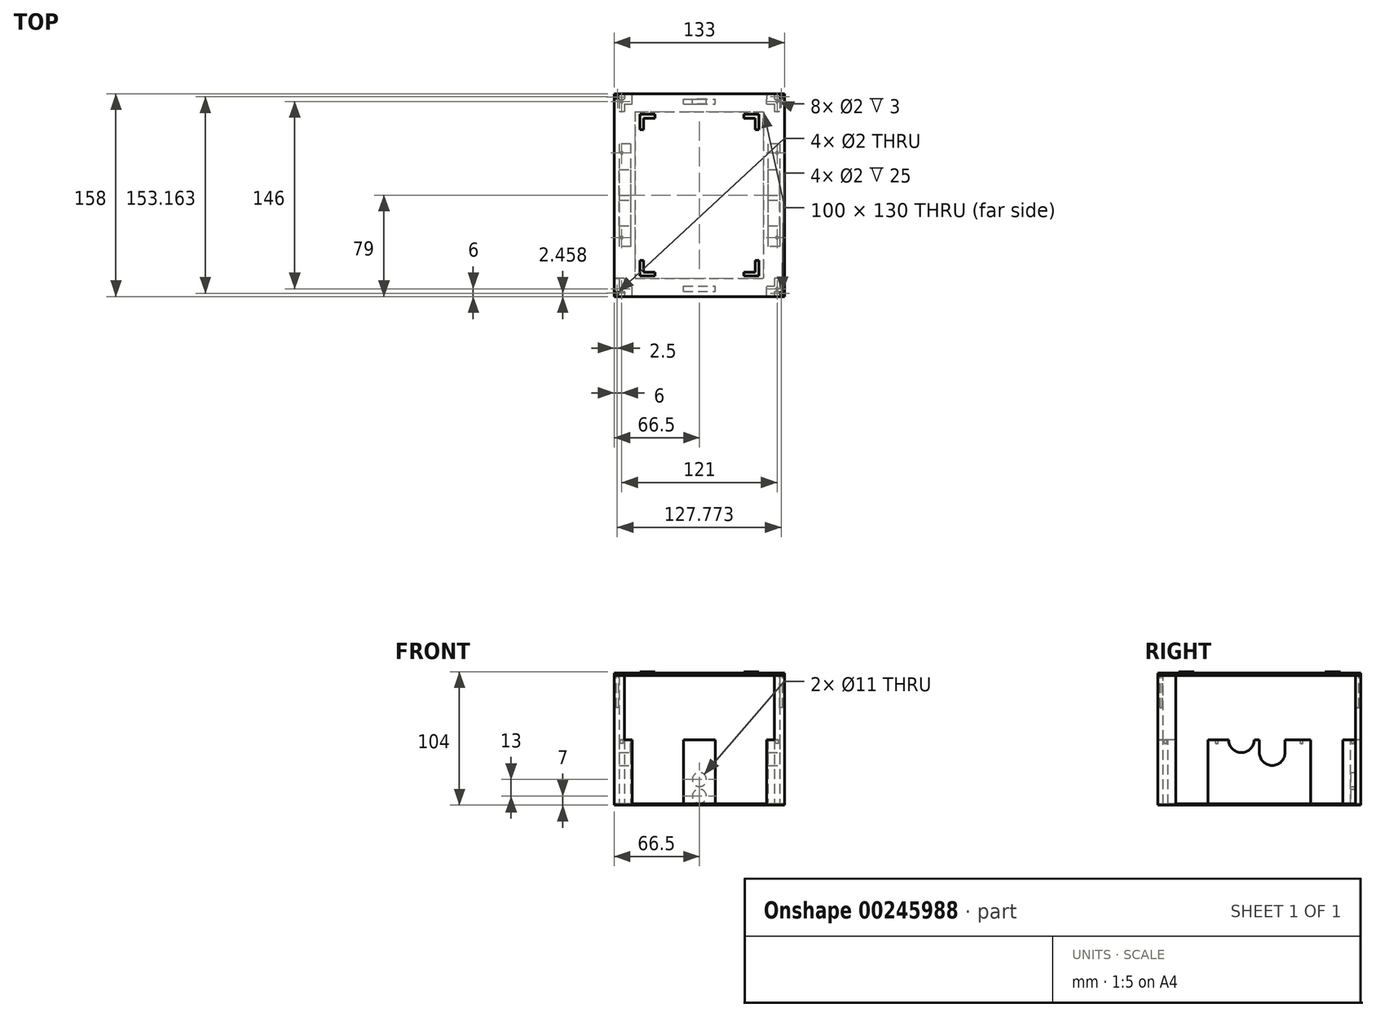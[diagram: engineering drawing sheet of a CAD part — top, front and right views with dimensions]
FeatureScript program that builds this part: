
annotation { "Feature Type Name" : "Feature", "Feature Type Description" : "" }
export const myFeature = defineFeature(function(context is Context, id is Id, definition is map)
    precondition{}
    {
        {
            var Q0;
            Q0=qCreatedBy(makeId("Top.planeOp"),FACE);
            var sketch = newSketch(context, id + "F0", { "sketchPlane" : qUnion([Q0])});
            skLineSegment(sketch, "E0.bottom", {"start": v(-66.5, 79) * mm, "end": v(66.5, 79) * mm});
            skLineSegment(sketch, "E0.top", {"start": v(-66.5, -79) * mm, "end": v(66.5, -79) * mm});
            skLineSegment(sketch, "E0.left", {"start": v(-66.5, 79) * mm, "end": v(-66.5, -79) * mm});
            skLineSegment(sketch, "E0.right", {"start": v(66.5, 79) * mm, "end": v(66.5, -79) * mm});
            skPoint(sketch, "E0.middle", {"position": v(0, 0) * mm});
            skLineSegment(sketch, "E1.bottom", {"start": v(-66.5, 79) * mm, "end": v(-66.5, 79) * mm});
            skLineSegment(sketch, "E1.top", {"start": v(-66.5, 79) * mm, "end": v(-66.5, 79) * mm});
            skLineSegment(sketch, "E1.left", {"start": v(-66.5, 79) * mm, "end": v(-66.5, 79) * mm});
            skLineSegment(sketch, "E1.right", {"start": v(-66.5, 79) * mm, "end": v(-66.5, 79) * mm});
            skLineSegment(sketch, "E2.bottom", {"start": v(-66.5, 79) * mm, "end": v(-62.5, 79) * mm});
            skLineSegment(sketch, "E2.top", {"start": v(-66.5, 79) * mm, "end": v(-62.5, 79) * mm});
            skLineSegment(sketch, "E2.right", {"start": v(-62.5, 79) * mm, "end": v(-62.5, 79) * mm});
            skSolve(sketch);
        }
        {
            var Q0;
            Q0=makeQuery(id+"F0.imprint","IMPRINT",FACE,{"disambiguationData":[TD([[makeQuery(id+"F0.imprint","IMPRINT",EDGE,{"derivedFrom":sQuery(id+"F0.wireOp",EDGE,"E0.bottom")}),-1.0]])]});
            extrude(context, id + "F1", {"entities" : qUnion([Q0]), "depth" : 1 * mm});
        }
        {
            var Q0;
            Q0=makeQuery(id+"F1.opExtrude","CAP_FACE",FACE,{"disambiguationData":[OSD([sQuery(id+"F0.wireOp",EDGE,"E0.bottom"),sQuery(id+"F0.wireOp",EDGE,"E0.top"),sQuery(id+"F0.wireOp",EDGE,"E0.left"),sQuery(id+"F0.wireOp",EDGE,"E0.right")])],"isStart":false});
            var sketch = newSketch(context, id + "F2", { "sketchPlane" : qUnion([Q0])});
            skLineSegment(sketch, "E3.bottom", {"start": v(-62.5, 75) * mm, "end": v(62.5, 75) * mm});
            skLineSegment(sketch, "E3.top", {"start": v(-62.5, -75) * mm, "end": v(62.5, -75) * mm});
            skLineSegment(sketch, "E3.left", {"start": v(-62.5, 75) * mm, "end": v(-62.5, -75) * mm});
            skLineSegment(sketch, "E3.right", {"start": v(62.5, 75) * mm, "end": v(62.5, -75) * mm});
            skPoint(sketch, "E3.middle", {"position": v(0, 0) * mm});
            skSolve(sketch);
        }
        {
            var Q0;
            Q0 = qSketchRegion(id + "F2", true);
            extrude(context, id + "F3", {"entities" : qUnion([Q0]), "operationType" : NewBodyOperationType.ADD, "depth" : 50 * mm});
        }
        {
            var Q0;
            Q0=makeQuery(id+"F3.opExtrude","CAP_FACE",FACE,{"disambiguationData":[OSD([sQuery(id+"F2.wireOp",EDGE,"E3.bottom"),sQuery(id+"F2.wireOp",EDGE,"E3.top"),sQuery(id+"F2.wireOp",EDGE,"E3.left"),sQuery(id+"F2.wireOp",EDGE,"E3.right")])],"isStart":false});
            var sketch = newSketch(context, id + "F4", { "sketchPlane" : qUnion([Q0])});
            skLineSegment(sketch, "E4.bottom", {"start": v(-58.5, 71) * mm, "end": v(58.5, 71) * mm});
            skLineSegment(sketch, "E4.top", {"start": v(-58.5, -71) * mm, "end": v(58.5, -71) * mm});
            skLineSegment(sketch, "E4.left", {"start": v(-58.5, 71) * mm, "end": v(-58.5, -71) * mm});
            skLineSegment(sketch, "E4.right", {"start": v(58.5, 71) * mm, "end": v(58.5, -71) * mm});
            skPoint(sketch, "E4.middle", {"position": v(0, 0) * mm});
            skSolve(sketch);
        }
        {
            var Q0;
            Q0=makeQuery(id+"F4.imprint","IMPRINT",FACE,{"disambiguationData":[TD([[makeQuery(id+"F4.imprint","IMPRINT",EDGE,{"derivedFrom":sQuery(id+"F4.wireOp",EDGE,"E4.bottom")}),-1.0]])]});
            extrude(context, id + "F5", {"entities" : qUnion([Q0]), "operationType" : NewBodyOperationType.REMOVE, "oppositeDirection" : true, "depth" : 50 * mm});
        }
        {
            var Q0;
            Q0=makeQuery(id+"F3.opExtrude","CAP_FACE",FACE,{"disambiguationData":[OSD([sQuery(id+"F2.wireOp",EDGE,"E3.bottom"),sQuery(id+"F2.wireOp",EDGE,"E3.top"),sQuery(id+"F2.wireOp",EDGE,"E3.left"),sQuery(id+"F2.wireOp",EDGE,"E3.right")])],"isStart":false});
            var sketch = newSketch(context, id + "F6", { "sketchPlane" : qUnion([Q0])});
            skCircle(sketch, "E5", {"center": v(-60.5, 73) * mm, "radius": 1 * mm});
            skCircle(sketch, "E6", {"center": v(-60.5, 33) * mm, "radius": 1 * mm});
            skCircle(sketch, "E7", {"center": v(60.5, 73) * mm, "radius": 1 * mm});
            skCircle(sketch, "E8", {"center": v(60.5, 33) * mm, "radius": 1 * mm});
            skCircle(sketch, "E9", {"center": v(-60.5, -33) * mm, "radius": 1 * mm});
            skCircle(sketch, "E10", {"center": v(60.5, -33) * mm, "radius": 1 * mm});
            skCircle(sketch, "E11", {"center": v(-60.5, -73) * mm, "radius": 1 * mm});
            skCircle(sketch, "E12", {"center": v(60.5, -73) * mm, "radius": 1 * mm});
            skSolve(sketch);
        }
        {
            var Q0;
            Q0=makeQuery(id+"F6.imprint","IMPRINT",FACE,{"disambiguationData":[TD([[makeQuery(id+"F6.imprint","IMPRINT",EDGE,{"derivedFrom":sQuery(id+"F6.wireOp",EDGE,"E5")}),1.0]])]});
            var Q1;
            Q1=makeQuery(id+"F6.imprint","IMPRINT",FACE,{"disambiguationData":[TD([[makeQuery(id+"F6.imprint","IMPRINT",EDGE,{"derivedFrom":sQuery(id+"F6.wireOp",EDGE,"E7")}),1.0]])]});
            var Q2;
            Q2=makeQuery(id+"F6.imprint","IMPRINT",FACE,{"disambiguationData":[TD([[makeQuery(id+"F6.imprint","IMPRINT",EDGE,{"derivedFrom":sQuery(id+"F6.wireOp",EDGE,"E8")}),1.0]])]});
            var Q3;
            Q3=makeQuery(id+"F6.imprint","IMPRINT",FACE,{"disambiguationData":[TD([[makeQuery(id+"F6.imprint","IMPRINT",EDGE,{"derivedFrom":sQuery(id+"F6.wireOp",EDGE,"E10")}),1.0]])]});
            var Q4;
            Q4=makeQuery(id+"F6.imprint","IMPRINT",FACE,{"disambiguationData":[TD([[makeQuery(id+"F6.imprint","IMPRINT",EDGE,{"derivedFrom":sQuery(id+"F6.wireOp",EDGE,"E12")}),1.0]])]});
            var Q5;
            Q5=makeQuery(id+"F6.imprint","IMPRINT",FACE,{"disambiguationData":[TD([[makeQuery(id+"F6.imprint","IMPRINT",EDGE,{"derivedFrom":sQuery(id+"F6.wireOp",EDGE,"E11")}),1.0]])]});
            var Q6;
            Q6=makeQuery(id+"F6.imprint","IMPRINT",FACE,{"disambiguationData":[TD([[makeQuery(id+"F6.imprint","IMPRINT",EDGE,{"derivedFrom":sQuery(id+"F6.wireOp",EDGE,"E9")}),1.0]])]});
            var Q7;
            Q7=makeQuery(id+"F6.imprint","IMPRINT",FACE,{"disambiguationData":[TD([[makeQuery(id+"F6.imprint","IMPRINT",EDGE,{"derivedFrom":sQuery(id+"F6.wireOp",EDGE,"E6")}),1.0]])]});
            extrude(context, id + "F7", {"entities" : qUnion([Q0, Q1, Q2, Q3, Q4, Q5, Q6, Q7]), "operationType" : NewBodyOperationType.REMOVE, "oppositeDirection" : true, "depth" : 3 * mm});
        }
        {
            var Q0;
            Q0=makeQuery(id+"F3.opExtrude","SWEPT_FACE",FACE,{"disambiguationData":[OSD([sQuery(id+"F2.wireOp",EDGE,"E3.right")])]});
            var sketch = newSketch(context, id + "F8", { "sketchPlane" : qUnion([Q0])});
            skLineSegment(sketch, "E13.bottom", {"start": v(0, 51) * mm, "end": v(20, 51) * mm});
            skLineSegment(sketch, "E13.top", {"start": v(0, 41) * mm, "end": v(20, 41) * mm});
            skLineSegment(sketch, "E13.left", {"start": v(0, 51) * mm, "end": v(0, 41) * mm});
            skLineSegment(sketch, "E13.right", {"start": v(20, 51) * mm, "end": v(20, 41) * mm});
            skSolve(sketch);
        }
        {
            var Q0;
            Q0=makeQuery(id+"F3.opExtrude","SWEPT_FACE",FACE,{"disambiguationData":[OSD([sQuery(id+"F2.wireOp",EDGE,"E3.right")])]});
            var sketch = newSketch(context, id + "F9", { "sketchPlane" : qUnion([Q0])});
            skCircle(sketch, "E14", {"center": v(10, 41) * mm, "radius": 10 * mm});
            skSolve(sketch);
        }
        {
            var Q0;
            Q0=makeQuery(id+"F8.imprint","IMPRINT",FACE,{"disambiguationData":[TD([[makeQuery(id+"F8.imprint","IMPRINT",EDGE,{"derivedFrom":sQuery(id+"F8.wireOp",EDGE,"E13.bottom")}),1.0]])]});
            extrude(context, id + "F10", {"entities" : qUnion([Q0]), "operationType" : NewBodyOperationType.REMOVE, "endBound" : BoundingType.THROUGH_ALL, "oppositeDirection" : true, "depth" : 25 * mm});
        }
        {
            var Q0;
            Q0=makeQuery(id+"F9.imprint","IMPRINT",FACE,{"disambiguationData":[TD([[makeQuery(id+"F9.imprint","IMPRINT",EDGE,{"derivedFrom":sQuery(id+"F9.wireOp",EDGE,"E14")}),1.0]])]});
            extrude(context, id + "F11", {"entities" : qUnion([Q0]), "operationType" : NewBodyOperationType.REMOVE, "endBound" : BoundingType.THROUGH_ALL, "oppositeDirection" : true, "depth" : 25 * mm});
        }
        {
            var Q0;
            Q0=makeQuery(id+"F3.opExtrude","SWEPT_FACE",FACE,{"disambiguationData":[OSD([sQuery(id+"F2.wireOp",EDGE,"E3.right")])]});
            var sketch = newSketch(context, id + "F12", { "sketchPlane" : qUnion([Q0])});
            skCircle(sketch, "E15", {"center": v(-13.97, 51) * mm, "radius": 10 * mm});
            skSolve(sketch);
        }
        {
            var Q0;
            {var subQ0=sQuery(id+"F12.wireOp",EDGE,"E15");var subQ1=sQuery(id+"F2.wireOp",EDGE,"E3.right");var subQ2=sQuery(id+"F2.wireOp",EDGE,"E3.top");var subQ3=makeQuery(id+"F10.boolean.opBoolean","SPLIT",EDGE,{"disambiguationData":[TD([makeQuery(id+"F3.opExtrude","SWEPT_FACE",FACE,{"disambiguationData":[OSD([subQ2])]})])],"derivedFrom":makeQuery(id+"F3.opExtrude","CAP_EDGE",EDGE,{"disambiguationData":[OSD([subQ1])],"isStart":false})});var subQ4=makeQuery(id+"F12.imprint","INTERSECT",VERTEX,{"disambiguationData":[OD(0.0)],"derivedFrom":[subQ3,subQ0]});Q0=makeQuery(id+"F12.imprint","IMPRINT",FACE,{"disambiguationData":[TD([[makeQuery(id+"F12.imprint","IMPRINT",EDGE,{"disambiguationData":[TD([[subQ4,-1.0]])],"derivedFrom":subQ0}),1.0]])]});}
            extrude(context, id + "F13", {"entities" : qUnion([Q0]), "operationType" : NewBodyOperationType.REMOVE, "endBound" : BoundingType.THROUGH_ALL, "oppositeDirection" : true, "depth" : 25 * mm});
        }
        {
            var Q0;
            Q0=makeQuery(id+"F3.opExtrude","SWEPT_FACE",FACE,{"disambiguationData":[OSD([sQuery(id+"F2.wireOp",EDGE,"E3.bottom")])]});
            var sketch = newSketch(context, id + "F14", { "sketchPlane" : qUnion([Q0])});
            skCircle(sketch, "E16", {"center": v(0, 7) * mm, "radius": 5.5 * mm});
            skCircle(sketch, "E17", {"center": v(0, 20) * mm, "radius": 5.5 * mm});
            skSolve(sketch);
        }
        {
            var Q0;
            Q0=makeQuery(id+"F14.imprint","IMPRINT",FACE,{"disambiguationData":[TD([[makeQuery(id+"F14.imprint","IMPRINT",EDGE,{"derivedFrom":sQuery(id+"F14.wireOp",EDGE,"E17")}),1.0]])]});
            var Q1;
            Q1=makeQuery(id+"F14.imprint","IMPRINT",FACE,{"disambiguationData":[TD([[makeQuery(id+"F14.imprint","IMPRINT",EDGE,{"derivedFrom":sQuery(id+"F14.wireOp",EDGE,"E16")}),1.0]])]});
            extrude(context, id + "F15", {"entities" : qUnion([Q0, Q1]), "operationType" : NewBodyOperationType.REMOVE, "oppositeDirection" : true, "depth" : 4 * mm});
        }
        {
            var Q0;
            Q0=makeQuery(id+"F3.opExtrude","SWEPT_FACE",FACE,{"disambiguationData":[OSD([sQuery(id+"F2.wireOp",EDGE,"E3.bottom")])]});
            var sketch = newSketch(context, id + "F16", { "sketchPlane" : qUnion([Q0])});
            skLineSegment(sketch, "E18.bottom", {"start": v(-52.5, 1) * mm, "end": v(-12.5, 1) * mm});
            skLineSegment(sketch, "E18.top", {"start": v(-52.5, 51) * mm, "end": v(-12.5, 51) * mm});
            skLineSegment(sketch, "E18.left", {"start": v(-52.5, 1) * mm, "end": v(-52.5, 51) * mm});
            skLineSegment(sketch, "E18.right", {"start": v(-12.5, 1) * mm, "end": v(-12.5, 51) * mm});
            skLineSegment(sketch, "E19.bottom", {"start": v(12.5, 51) * mm, "end": v(52.5, 51) * mm});
            skLineSegment(sketch, "E19.top", {"start": v(12.5, 1) * mm, "end": v(52.5, 1) * mm});
            skLineSegment(sketch, "E19.left", {"start": v(12.5, 51) * mm, "end": v(12.5, 1) * mm});
            skLineSegment(sketch, "E19.right", {"start": v(52.5, 51) * mm, "end": v(52.5, 1) * mm});
            skSolve(sketch);
        }
        {
            var Q0;
            Q0=makeQuery(id+"F16.imprint","IMPRINT",FACE,{"disambiguationData":[TD([[makeQuery(id+"F16.imprint","IMPRINT",EDGE,{"derivedFrom":sQuery(id+"F16.wireOp",EDGE,"E18.bottom")}),-1.0]])]});
            var Q1;
            Q1=makeQuery(id+"F16.imprint","IMPRINT",FACE,{"disambiguationData":[TD([[makeQuery(id+"F16.imprint","IMPRINT",EDGE,{"derivedFrom":sQuery(id+"F16.wireOp",EDGE,"E19.bottom")}),1.0]])]});
            extrude(context, id + "F17", {"entities" : qUnion([Q0, Q1]), "operationType" : NewBodyOperationType.REMOVE, "endBound" : BoundingType.THROUGH_ALL, "oppositeDirection" : true, "depth" : 25 * mm});
        }
        {
            var Q0;
            Q0=makeQuery(id+"F3.opExtrude","SWEPT_FACE",FACE,{"disambiguationData":[OSD([sQuery(id+"F2.wireOp",EDGE,"E3.left")])]});
            var sketch = newSketch(context, id + "F18", { "sketchPlane" : qUnion([Q0])});
            skLineSegment(sketch, "E20.bottom", {"start": v(-65, 51) * mm, "end": v(-40, 51) * mm});
            skLineSegment(sketch, "E20.top", {"start": v(-65, 1) * mm, "end": v(-40, 1) * mm});
            skLineSegment(sketch, "E20.left", {"start": v(-65, 51) * mm, "end": v(-65, 1) * mm});
            skLineSegment(sketch, "E20.right", {"start": v(-40, 51) * mm, "end": v(-40, 1) * mm});
            skLineSegment(sketch, "E21.bottom", {"start": v(40, 51) * mm, "end": v(65, 51) * mm});
            skLineSegment(sketch, "E21.top", {"start": v(40, 1) * mm, "end": v(65, 1) * mm});
            skLineSegment(sketch, "E21.left", {"start": v(40, 51) * mm, "end": v(40, 1) * mm});
            skLineSegment(sketch, "E21.right", {"start": v(65, 51) * mm, "end": v(65, 1) * mm});
            skSolve(sketch);
        }
        {
            var Q0;
            Q0=makeQuery(id+"F18.imprint","IMPRINT",FACE,{"disambiguationData":[TD([[makeQuery(id+"F18.imprint","IMPRINT",EDGE,{"derivedFrom":sQuery(id+"F18.wireOp",EDGE,"E20.bottom")}),-1.0]])]});
            var Q1;
            Q1=makeQuery(id+"F18.imprint","IMPRINT",FACE,{"disambiguationData":[TD([[makeQuery(id+"F18.imprint","IMPRINT",EDGE,{"derivedFrom":sQuery(id+"F18.wireOp",EDGE,"E21.bottom")}),-1.0]])]});
            extrude(context, id + "F19", {"entities" : qUnion([Q0, Q1]), "operationType" : NewBodyOperationType.REMOVE, "endBound" : BoundingType.THROUGH_ALL, "oppositeDirection" : true, "depth" : 25 * mm});
        }
        {
            var Q0;
            Q0=makeQuery(id+"F19.boolean.opBoolean","MERGE",FACE,{"derivedFrom":[makeQuery(id+"F17.boolean.opBoolean","MERGE",FACE,{"derivedFrom":[makeQuery(id+"F1.opExtrude","CAP_FACE",FACE,{"disambiguationData":[OSD([sQuery(id+"F0.wireOp",EDGE,"E0.bottom"),sQuery(id+"F0.wireOp",EDGE,"E0.top"),sQuery(id+"F0.wireOp",EDGE,"E0.left"),sQuery(id+"F0.wireOp",EDGE,"E0.right"),sQuery(id+"F0.wireOp",EDGE,"E2.top")])],"isStart":false}),makeQuery(id+"F5.boolean.opBoolean","COPY",FACE,{"derivedFrom":makeQuery(id+"F5.opExtrude","CAP_FACE",FACE,{"disambiguationData":[OSD([sQuery(id+"F4.wireOp",EDGE,"E4.bottom"),sQuery(id+"F4.wireOp",EDGE,"E4.top"),sQuery(id+"F4.wireOp",EDGE,"E4.left"),sQuery(id+"F4.wireOp",EDGE,"E4.right")])],"isStart":false})}),makeQuery(id+"F17.opExtrude","SWEPT_FACE",FACE,{"disambiguationData":[OSD([sQuery(id+"F16.wireOp",EDGE,"E18.bottom")])]}),makeQuery(id+"F17.opExtrude","SWEPT_FACE",FACE,{"disambiguationData":[OSD([sQuery(id+"F16.wireOp",EDGE,"E19.top")])]})]}),makeQuery(id+"F19.opExtrude","SWEPT_FACE",FACE,{"disambiguationData":[OSD([sQuery(id+"F18.wireOp",EDGE,"E20.top")])]}),makeQuery(id+"F19.opExtrude","SWEPT_FACE",FACE,{"disambiguationData":[OSD([sQuery(id+"F18.wireOp",EDGE,"E21.top")])]})]});
            var sketch = newSketch(context, id + "F20", { "sketchPlane" : qUnion([Q0])});
            skLineSegment(sketch, "E22.bottom", {"start": v(-66.5, 79) * mm, "end": v(-52.5, 79) * mm});
            skLineSegment(sketch, "E22.top", {"start": v(-66.5, 75) * mm, "end": v(-52.5, 75) * mm});
            skLineSegment(sketch, "E22.left", {"start": v(-66.5, 79) * mm, "end": v(-66.5, 75) * mm});
            skLineSegment(sketch, "E22.right", {"start": v(-52.5, 79) * mm, "end": v(-52.5, 75) * mm});
            skLineSegment(sketch, "E23.bottom", {"start": v(-66.5, 75) * mm, "end": v(-62.5, 75) * mm});
            skLineSegment(sketch, "E23.top", {"start": v(-66.5, 65) * mm, "end": v(-62.5, 65) * mm});
            skLineSegment(sketch, "E23.left", {"start": v(-66.5, 75) * mm, "end": v(-66.5, 65) * mm});
            skLineSegment(sketch, "E23.right", {"start": v(-62.5, 75) * mm, "end": v(-62.5, 65) * mm});
            skLineSegment(sketch, "E24.bottom", {"start": v(52.52, 79) * mm, "end": v(66.5, 79) * mm});
            skLineSegment(sketch, "E24.top", {"start": v(52.52, 75) * mm, "end": v(66.5, 75) * mm});
            skLineSegment(sketch, "E24.left", {"start": v(52.52, 79) * mm, "end": v(52.52, 75) * mm});
            skLineSegment(sketch, "E24.right", {"start": v(66.5, 79) * mm, "end": v(66.5, 75) * mm});
            skLineSegment(sketch, "E25.bottom", {"start": v(62.5, 75) * mm, "end": v(66.5, 75) * mm});
            skLineSegment(sketch, "E25.top", {"start": v(62.5, 64.97) * mm, "end": v(66.5, 64.97) * mm});
            skLineSegment(sketch, "E25.left", {"start": v(62.5, 75) * mm, "end": v(62.5, 64.97) * mm});
            skLineSegment(sketch, "E25.right", {"start": v(66.5, 75) * mm, "end": v(66.5, 64.97) * mm});
            skLineSegment(sketch, "E26.bottom", {"start": v(62.5, -65) * mm, "end": v(66.5, -65) * mm});
            skLineSegment(sketch, "E26.top", {"start": v(62.5, -79) * mm, "end": v(66.5, -79) * mm});
            skLineSegment(sketch, "E26.left", {"start": v(62.5, -65) * mm, "end": v(62.5, -79) * mm});
            skLineSegment(sketch, "E26.right", {"start": v(66.5, -65) * mm, "end": v(66.5, -79) * mm});
            skLineSegment(sketch, "E27.bottom", {"start": v(52.5, -75) * mm, "end": v(62.5, -75) * mm});
            skLineSegment(sketch, "E27.top", {"start": v(52.5, -79) * mm, "end": v(62.5, -79) * mm});
            skLineSegment(sketch, "E27.left", {"start": v(52.5, -75) * mm, "end": v(52.5, -79) * mm});
            skLineSegment(sketch, "E27.right", {"start": v(62.5, -75) * mm, "end": v(62.5, -79) * mm});
            skLineSegment(sketch, "E28.bottom", {"start": v(-66.5, -65) * mm, "end": v(-62.5, -65) * mm});
            skLineSegment(sketch, "E28.top", {"start": v(-66.5, -79) * mm, "end": v(-62.5, -79) * mm});
            skLineSegment(sketch, "E28.left", {"start": v(-66.5, -65) * mm, "end": v(-66.5, -79) * mm});
            skLineSegment(sketch, "E28.right", {"start": v(-62.5, -65) * mm, "end": v(-62.5, -79) * mm});
            skLineSegment(sketch, "E29.bottom", {"start": v(-62.5, -75) * mm, "end": v(-52.5, -75) * mm});
            skLineSegment(sketch, "E29.top", {"start": v(-62.5, -79) * mm, "end": v(-52.5, -79) * mm});
            skLineSegment(sketch, "E29.left", {"start": v(-62.5, -75) * mm, "end": v(-62.5, -79) * mm});
            skLineSegment(sketch, "E29.right", {"start": v(-52.5, -75) * mm, "end": v(-52.5, -79) * mm});
            skSolve(sketch);
        }
        {
            var Q0;
            Q0=makeQuery(id+"F20.imprint","IMPRINT",FACE,{"disambiguationData":[TD([[makeQuery(id+"F20.imprint","IMPRINT",EDGE,{"derivedFrom":sQuery(id+"F20.wireOp",EDGE,"E28.bottom")}),-1.0]])]});
            var Q1;
            Q1=makeQuery(id+"F20.imprint","IMPRINT",FACE,{"disambiguationData":[TD([[makeQuery(id+"F20.imprint","IMPRINT",EDGE,{"derivedFrom":sQuery(id+"F20.wireOp",EDGE,"E29.bottom")}),-1.0]])]});
            var Q2;
            Q2=makeQuery(id+"F20.imprint","IMPRINT",FACE,{"disambiguationData":[TD([[makeQuery(id+"F20.imprint","IMPRINT",EDGE,{"derivedFrom":sQuery(id+"F20.wireOp",EDGE,"E27.bottom")}),-1.0]])]});
            var Q3;
            Q3=makeQuery(id+"F20.imprint","IMPRINT",FACE,{"disambiguationData":[TD([[makeQuery(id+"F20.imprint","IMPRINT",EDGE,{"derivedFrom":sQuery(id+"F20.wireOp",EDGE,"E26.bottom")}),-1.0]])]});
            var Q4;
            Q4=makeQuery(id+"F20.imprint","IMPRINT",FACE,{"disambiguationData":[TD([[makeQuery(id+"F20.imprint","IMPRINT",EDGE,{"derivedFrom":sQuery(id+"F20.wireOp",EDGE,"E22.bottom")}),-1.0]])]});
            var Q5;
            Q5=makeQuery(id+"F20.imprint","IMPRINT",FACE,{"disambiguationData":[TD([[makeQuery(id+"F20.imprint","IMPRINT",EDGE,{"derivedFrom":sQuery(id+"F20.wireOp",EDGE,"E23.bottom")}),-1.0]])]});
            var Q6;
            Q6=makeQuery(id+"F20.imprint","IMPRINT",FACE,{"disambiguationData":[TD([[makeQuery(id+"F20.imprint","IMPRINT",EDGE,{"derivedFrom":sQuery(id+"F20.wireOp",EDGE,"E24.bottom")}),-1.0]])]});
            var Q7;
            {var subQ6=sQuery(id+"F20.wireOp",EDGE,"E25.bottom");Q7=makeQuery(id+"F20.imprint","IMPRINT",FACE,{"disambiguationData":[TD([[makeQuery(id+"F20.imprint","IMPRINT",EDGE,{"derivedFrom":subQ6}),-1.0]])]});}
            extrude(context, id + "F21", {"entities" : qUnion([Q0, Q1, Q2, Q3, Q4, Q5, Q6, Q7]), "operationType" : NewBodyOperationType.ADD, "depth" : 100 * mm});
        }
        {
            var Q0;
            Q0=makeQuery(id+"F21.opExtrude","CAP_FACE",FACE,{"disambiguationData":[OSD([sQuery(id+"F20.wireOp",EDGE,"E22.bottom"),sQuery(id+"F20.wireOp",EDGE,"E22.top"),sQuery(id+"F20.wireOp",EDGE,"E22.left"),sQuery(id+"F20.wireOp",EDGE,"E22.right"),sQuery(id+"F20.wireOp",EDGE,"E23.top"),sQuery(id+"F20.wireOp",EDGE,"E23.left"),sQuery(id+"F20.wireOp",EDGE,"E23.right")])],"isStart":false});
            var sketch = newSketch(context, id + "F22", { "sketchPlane" : qUnion([Q0])});
            skCircle(sketch, "E30", {"center": v(-63.91, 76.41) * mm, "radius": 1 * mm});
            skCircle(sketch, "E31", {"center": v(63.67, 76.62) * mm, "radius": 1 * mm});
            skCircle(sketch, "E32", {"center": v(63.77, -76.54) * mm, "radius": 1 * mm});
            skCircle(sketch, "E33", {"center": v(-64, -76.32) * mm, "radius": 1 * mm});
            skSolve(sketch);
        }
        {
            var Q0;
            Q0=makeQuery(id+"F22.imprint","IMPRINT",FACE,{"disambiguationData":[TD([[makeQuery(id+"F22.imprint","IMPRINT",EDGE,{"derivedFrom":sQuery(id+"F22.wireOp",EDGE,"E30")}),1.0]])]});
            var Q1;
            Q1=makeQuery(id+"F22.imprint","IMPRINT",FACE,{"disambiguationData":[TD([[makeQuery(id+"F22.imprint","IMPRINT",EDGE,{"derivedFrom":sQuery(id+"F22.wireOp",EDGE,"E31")}),1.0]])]});
            var Q2;
            Q2=makeQuery(id+"F22.imprint","IMPRINT",FACE,{"disambiguationData":[TD([[makeQuery(id+"F22.imprint","IMPRINT",EDGE,{"derivedFrom":sQuery(id+"F22.wireOp",EDGE,"E32")}),1.0]])]});
            var Q3;
            Q3=makeQuery(id+"F22.imprint","IMPRINT",FACE,{"disambiguationData":[TD([[makeQuery(id+"F22.imprint","IMPRINT",EDGE,{"derivedFrom":sQuery(id+"F22.wireOp",EDGE,"E33")}),1.0]])]});
            extrude(context, id + "F23", {"entities" : qUnion([Q0, Q1, Q2, Q3]), "operationType" : NewBodyOperationType.REMOVE, "oppositeDirection" : true, "depth" : 25 * mm});
        }
        {
            var Q0;
            {var subQ3=sQuery(id+"F4.wireOp",EDGE,"E4.right");var subQ4=makeQuery(id+"F5.boolean.opBoolean","COPY",FACE,{"derivedFrom":makeQuery(id+"F5.opExtrude","SWEPT_FACE",FACE,{"disambiguationData":[OSD([subQ3])]})});Q0=makeQuery(id+"F19.boolean.opBoolean","SPLIT",FACE,{"disambiguationData":[TD([makeQuery(id+"F19.opExtrude","SWEPT_FACE",FACE,{"disambiguationData":[OSD([sQuery(id+"F18.wireOp",EDGE,"E20.right")])]})])],"derivedFrom":subQ4});}
            extrude(context, id + "F24", {"entities" : qUnion([Q0]), "operationType" : NewBodyOperationType.ADD, "depth" : 5 * mm});
        }
        {
            var Q0;
            {var subQ4=sQuery(id+"F4.wireOp",EDGE,"E4.left");var subQ5=makeQuery(id+"F5.boolean.opBoolean","COPY",FACE,{"derivedFrom":makeQuery(id+"F5.opExtrude","SWEPT_FACE",FACE,{"disambiguationData":[OSD([subQ4])]})});Q0=makeQuery(id+"F19.boolean.opBoolean","SPLIT",FACE,{"disambiguationData":[TD([makeQuery(id+"F19.opExtrude","SWEPT_FACE",FACE,{"disambiguationData":[OSD([sQuery(id+"F18.wireOp",EDGE,"E20.right")])]})])],"derivedFrom":subQ5});}
            extrude(context, id + "F25", {"entities" : qUnion([Q0]), "operationType" : NewBodyOperationType.ADD, "depth" : 5 * mm});
        }
        {
            var Q0;
            Q0=makeQuery(id+"F19.boolean.opBoolean","MERGE",FACE,{"derivedFrom":[makeQuery(id+"F17.boolean.opBoolean","MERGE",FACE,{"derivedFrom":[makeQuery(id+"F1.opExtrude","CAP_FACE",FACE,{"disambiguationData":[OSD([sQuery(id+"F0.wireOp",EDGE,"E0.bottom"),sQuery(id+"F0.wireOp",EDGE,"E0.top"),sQuery(id+"F0.wireOp",EDGE,"E0.left"),sQuery(id+"F0.wireOp",EDGE,"E0.right"),sQuery(id+"F0.wireOp",EDGE,"E2.top")])],"isStart":false}),makeQuery(id+"F5.boolean.opBoolean","COPY",FACE,{"derivedFrom":makeQuery(id+"F5.opExtrude","CAP_FACE",FACE,{"disambiguationData":[OSD([sQuery(id+"F4.wireOp",EDGE,"E4.bottom"),sQuery(id+"F4.wireOp",EDGE,"E4.top"),sQuery(id+"F4.wireOp",EDGE,"E4.left"),sQuery(id+"F4.wireOp",EDGE,"E4.right")])],"isStart":false})}),makeQuery(id+"F17.opExtrude","SWEPT_FACE",FACE,{"disambiguationData":[OSD([sQuery(id+"F16.wireOp",EDGE,"E18.bottom")])]}),makeQuery(id+"F17.opExtrude","SWEPT_FACE",FACE,{"disambiguationData":[OSD([sQuery(id+"F16.wireOp",EDGE,"E19.top")])]})]}),makeQuery(id+"F19.opExtrude","SWEPT_FACE",FACE,{"disambiguationData":[OSD([sQuery(id+"F18.wireOp",EDGE,"E20.top")])]}),makeQuery(id+"F19.opExtrude","SWEPT_FACE",FACE,{"disambiguationData":[OSD([sQuery(id+"F18.wireOp",EDGE,"E21.top")])]})]});
            var sketch = newSketch(context, id + "F26", { "sketchPlane" : qUnion([Q0])});
            skLineSegment(sketch, "E34.bottom", {"start": v(-50, 65) * mm, "end": v(50, 65) * mm});
            skLineSegment(sketch, "E34.top", {"start": v(-50, -65) * mm, "end": v(50, -65) * mm});
            skLineSegment(sketch, "E34.left", {"start": v(-50, 65) * mm, "end": v(-50, -65) * mm});
            skLineSegment(sketch, "E34.right", {"start": v(50, 65) * mm, "end": v(50, -65) * mm});
            skPoint(sketch, "E34.middle", {"position": v(0, 0) * mm});
            skSolve(sketch);
        }
        {
            var Q0;
            Q0=makeQuery(id+"F26.imprint","IMPRINT",FACE,{"disambiguationData":[TD([[makeQuery(id+"F26.imprint","IMPRINT",EDGE,{"derivedFrom":sQuery(id+"F26.wireOp",EDGE,"E34.bottom")}),-1.0]])]});
            extrude(context, id + "F27", {"entities" : qUnion([Q0]), "operationType" : NewBodyOperationType.REMOVE, "endBound" : BoundingType.THROUGH_ALL, "oppositeDirection" : true, "depth" : 25 * mm});
        }
        {
            var Q0;
            Q0=makeQuery(id+"F21.boolean.opBoolean","MERGE",FACE,{"derivedFrom":[makeQuery(id+"F1.opExtrude","SWEPT_FACE",FACE,{"disambiguationData":[OSD([sQuery(id+"F0.wireOp",EDGE,"E0.top")])]}),makeQuery(id+"F21.opExtrude","SWEPT_FACE",FACE,{"disambiguationData":[OSD([sQuery(id+"F20.wireOp",EDGE,"E26.top"),sQuery(id+"F20.wireOp",EDGE,"E27.top")])]}),makeQuery(id+"F21.opExtrude","SWEPT_FACE",FACE,{"disambiguationData":[OSD([sQuery(id+"F20.wireOp",EDGE,"E28.top"),sQuery(id+"F20.wireOp",EDGE,"E29.top")])]})]});
            var sketch = newSketch(context, id + "F28", { "sketchPlane" : qUnion([Q0])});
            skLineSegment(sketch, "E35.bottom", {"start": v(-52.5, 101) * mm, "end": v(-58.5, 101) * mm});
            skLineSegment(sketch, "E35.top", {"start": v(-52.5, 51) * mm, "end": v(-58.5, 51) * mm});
            skLineSegment(sketch, "E35.left", {"start": v(-52.5, 101) * mm, "end": v(-52.5, 51) * mm});
            skLineSegment(sketch, "E35.right", {"start": v(-58.5, 101) * mm, "end": v(-58.5, 51) * mm});
            skLineSegment(sketch, "E36.bottom", {"start": v(52.5, 101) * mm, "end": v(58.5, 101) * mm});
            skLineSegment(sketch, "E36.top", {"start": v(52.5, 51) * mm, "end": v(58.5, 51) * mm});
            skLineSegment(sketch, "E36.left", {"start": v(52.5, 101) * mm, "end": v(52.5, 51) * mm});
            skLineSegment(sketch, "E36.right", {"start": v(58.5, 101) * mm, "end": v(58.5, 51) * mm});
            skSolve(sketch);
        }
        {
            var Q0;
            Q0=makeQuery(id+"F28.imprint","IMPRINT",FACE,{"disambiguationData":[TD([[makeQuery(id+"F28.imprint","IMPRINT",EDGE,{"derivedFrom":sQuery(id+"F28.wireOp",EDGE,"E35.bottom")}),-1.0]])]});
            var Q1;
            Q1=makeQuery(id+"F28.imprint","IMPRINT",FACE,{"disambiguationData":[TD([[makeQuery(id+"F28.imprint","IMPRINT",EDGE,{"derivedFrom":sQuery(id+"F28.wireOp",EDGE,"E36.bottom")}),-1.0]])]});
            extrude(context, id + "F29", {"entities" : qUnion([Q0, Q1]), "operationType" : NewBodyOperationType.REMOVE, "endBound" : BoundingType.THROUGH_ALL, "oppositeDirection" : true, "depth" : 25 * mm});
        }
        {
            var Q0;
            Q0=makeQuery(id+"F21.opExtrude","CAP_FACE",FACE,{"disambiguationData":[OSD([sQuery(id+"F20.wireOp",EDGE,"E28.bottom"),sQuery(id+"F20.wireOp",EDGE,"E28.top"),sQuery(id+"F20.wireOp",EDGE,"E28.left"),sQuery(id+"F20.wireOp",EDGE,"E28.right"),sQuery(id+"F20.wireOp",EDGE,"E29.bottom"),sQuery(id+"F20.wireOp",EDGE,"E29.top"),sQuery(id+"F20.wireOp",EDGE,"E29.right")])],"isStart":false});
            cPlane(context, id + "F30", {"entities" : qUnion([Q0]), "cplaneType" : CPlaneType.OFFSET, "offset" : 0 * mm, "width" : 150 * mm, "height" : 150 * mm});
        }
        {
            var Q0;
            Q0=qCreatedBy(id+"F30.planeOp",FACE);
            var sketch = newSketch(context, id + "F31", { "sketchPlane" : qUnion([Q0])});
            skLineSegment(sketch, "E37", {"start": v(-66.5, 79) * mm, "end": v(66.5, 79) * mm});
            skLineSegment(sketch, "E38", {"start": v(66.5, -79) * mm, "end": v(-66.5, -79) * mm});
            skLineSegment(sketch, "E39", {"start": v(-66.5, -79) * mm, "end": v(-66.5, 79) * mm});
            skLineSegment(sketch, "E40", {"start": v(66.5, 79) * mm, "end": v(66.5, -79) * mm});
            skCircle(sketch, "E41.0", {"center": v(-63.91, 76.41) * mm, "radius": 1 * mm});
            skCircle(sketch, "E41.1", {"center": v(63.67, 76.62) * mm, "radius": 1 * mm});
            skCircle(sketch, "E41.2", {"center": v(-64, -76.32) * mm, "radius": 1 * mm});
            skCircle(sketch, "E41.3", {"center": v(63.77, -76.54) * mm, "radius": 1 * mm});
            skPoint(sketch, "E42.middle", {"position": v(0, 0) * mm});
            skLineSegment(sketch, "E43", {"start": v(-43.5, 51) * mm, "end": v(-46.5, 51) * mm});
            skLineSegment(sketch, "E44", {"start": v(-46.5, 51) * mm, "end": v(-46.5, 63) * mm});
            skLineSegment(sketch, "E45", {"start": v(-46.5, 63) * mm, "end": v(-34.5, 63) * mm});
            skLineSegment(sketch, "E46", {"start": v(-34.5, 63) * mm, "end": v(-34.5, 60) * mm});
            skLineSegment(sketch, "E47", {"start": v(-34.5, 60) * mm, "end": v(-43.5, 60) * mm});
            skLineSegment(sketch, "E48", {"start": v(-43.5, 60) * mm, "end": v(-43.5, 51) * mm});
            skLineSegment(sketch, "E49.MirrorCS", {"start": v(46.5, 63) * mm, "end": v(34.5, 63) * mm});
            skLineSegment(sketch, "E50.MirrorCS", {"start": v(46.5, 51) * mm, "end": v(46.5, 63) * mm});
            skLineSegment(sketch, "E51.MirrorCS", {"start": v(43.5, 51) * mm, "end": v(46.5, 51) * mm});
            skLineSegment(sketch, "E52.MirrorCS", {"start": v(43.5, 60) * mm, "end": v(43.5, 51) * mm});
            skLineSegment(sketch, "E53.MirrorCS", {"start": v(34.5, 60) * mm, "end": v(43.5, 60) * mm});
            skLineSegment(sketch, "E54.MirrorCS", {"start": v(34.5, 63) * mm, "end": v(34.5, 60) * mm});
            skLineSegment(sketch, "E55.MirrorCS", {"start": v(-34.5, -63) * mm, "end": v(-34.5, -60) * mm});
            skLineSegment(sketch, "E56.MirrorCS", {"start": v(43.5, -51) * mm, "end": v(46.5, -51) * mm});
            skLineSegment(sketch, "E57.MirrorCS", {"start": v(-43.5, -51) * mm, "end": v(-46.5, -51) * mm});
            skLineSegment(sketch, "E58.MirrorCS", {"start": v(34.5, -63) * mm, "end": v(34.5, -60) * mm});
            skLineSegment(sketch, "E59.MirrorCS", {"start": v(-46.5, -51) * mm, "end": v(-46.5, -63) * mm});
            skLineSegment(sketch, "E60.MirrorCS", {"start": v(-43.5, -60) * mm, "end": v(-43.5, -51) * mm});
            skLineSegment(sketch, "E61.MirrorCS", {"start": v(43.5, -60) * mm, "end": v(43.5, -51) * mm});
            skLineSegment(sketch, "E62.MirrorCS", {"start": v(-46.5, -63) * mm, "end": v(-34.5, -63) * mm});
            skLineSegment(sketch, "E63.MirrorCS", {"start": v(46.5, -63) * mm, "end": v(34.5, -63) * mm});
            skLineSegment(sketch, "E64.MirrorCS", {"start": v(-34.5, -60) * mm, "end": v(-43.5, -60) * mm});
            skLineSegment(sketch, "E65.MirrorCS", {"start": v(46.5, -51) * mm, "end": v(46.5, -63) * mm});
            skLineSegment(sketch, "E66.MirrorCS", {"start": v(34.5, -60) * mm, "end": v(43.5, -60) * mm});
            skSolve(sketch);
        }
        {
            var Q0;
            Q0=makeQuery(id+"F31.imprint","IMPRINT",FACE,{"disambiguationData":[TD([[makeQuery(id+"F31.imprint","IMPRINT",EDGE,{"derivedFrom":sQuery(id+"F31.wireOp",EDGE,"E37")}),-1.0]])]});
            extrude(context, id + "F32", {"entities" : qUnion([Q0]), "depth" : 2 * mm, "offsetDistance" : 25 * mm});
        }
        {
            var Q0;
            Q0=makeQuery(id+"F31.imprint","IMPRINT",FACE,{"disambiguationData":[TD([[makeQuery(id+"F31.imprint","IMPRINT",EDGE,{"derivedFrom":sQuery(id+"F31.wireOp",EDGE,"E43")}),-1.0]])]});
            var Q1;
            Q1=makeQuery(id+"F31.imprint","IMPRINT",FACE,{"disambiguationData":[TD([[makeQuery(id+"F31.imprint","IMPRINT",EDGE,{"derivedFrom":sQuery(id+"F31.wireOp",EDGE,"E49.MirrorCS")}),1.0]])]});
            var Q2;
            Q2=makeQuery(id+"F31.imprint","IMPRINT",FACE,{"disambiguationData":[TD([[makeQuery(id+"F31.imprint","IMPRINT",EDGE,{"derivedFrom":sQuery(id+"F31.wireOp",EDGE,"E55.MirrorCS")}),1.0]])]});
            var Q3;
            Q3=makeQuery(id+"F31.imprint","IMPRINT",FACE,{"disambiguationData":[TD([[makeQuery(id+"F31.imprint","IMPRINT",EDGE,{"derivedFrom":sQuery(id+"F31.wireOp",EDGE,"E56.MirrorCS")}),-1.0]])]});
            extrude(context, id + "F33", {"entities" : qUnion([Q0, Q1, Q2, Q3]), "operationType" : NewBodyOperationType.ADD, "depth" : 3 * mm, "offsetDistance" : 25 * mm});
        }
    });
